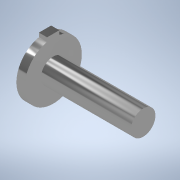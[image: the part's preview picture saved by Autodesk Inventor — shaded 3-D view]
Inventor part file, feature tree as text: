
AUTODESK INVENTOR PART (.ipt)
format: ipt  version: 2021 (Build 250183000, 183)  size: 129,536 bytes
history: native  units: in
note: dims shown in document units (in); Inventor stores cm internally (conversion verified against a paired STEP export)
features: extrude x5, sketch x3
ambient origin geometry x8: Origin, YZ Plane, XZ Plane, XY Plane, X Axis, Y Axis, Z Axis, Center Point
bodies: Solid1 (feature_tree)
feature tree (8):
  sketch  "Sketch1"  dims[d0=0.1181in d1=0.2756in]
  extrude  "Extrusion1"  Depth=0.2756in
  extrude  "Extrusion2"  Depth=0.0394in TaperAngle=0.0deg
  sketch  "Sketch2"  dims[d4=0.4331in d5=0.0in d6=0.0394in d7=0.0in]
  extrude  "Extrusion3"  Depth=0.0787in
  extrude  "Extrusion4"  Depth=0.0394in TaperAngle=0.0deg
  extrude  "Extrusion5"  Depth=0.0589in
  sketch  "Sketch3"  dims[d8=0.0787in d9=0.0in d10=0.0787in d11=0.0394in d12=0.0in d13=0.0589in d14=0.0394in d15=0.0in d16=0.1181in]
